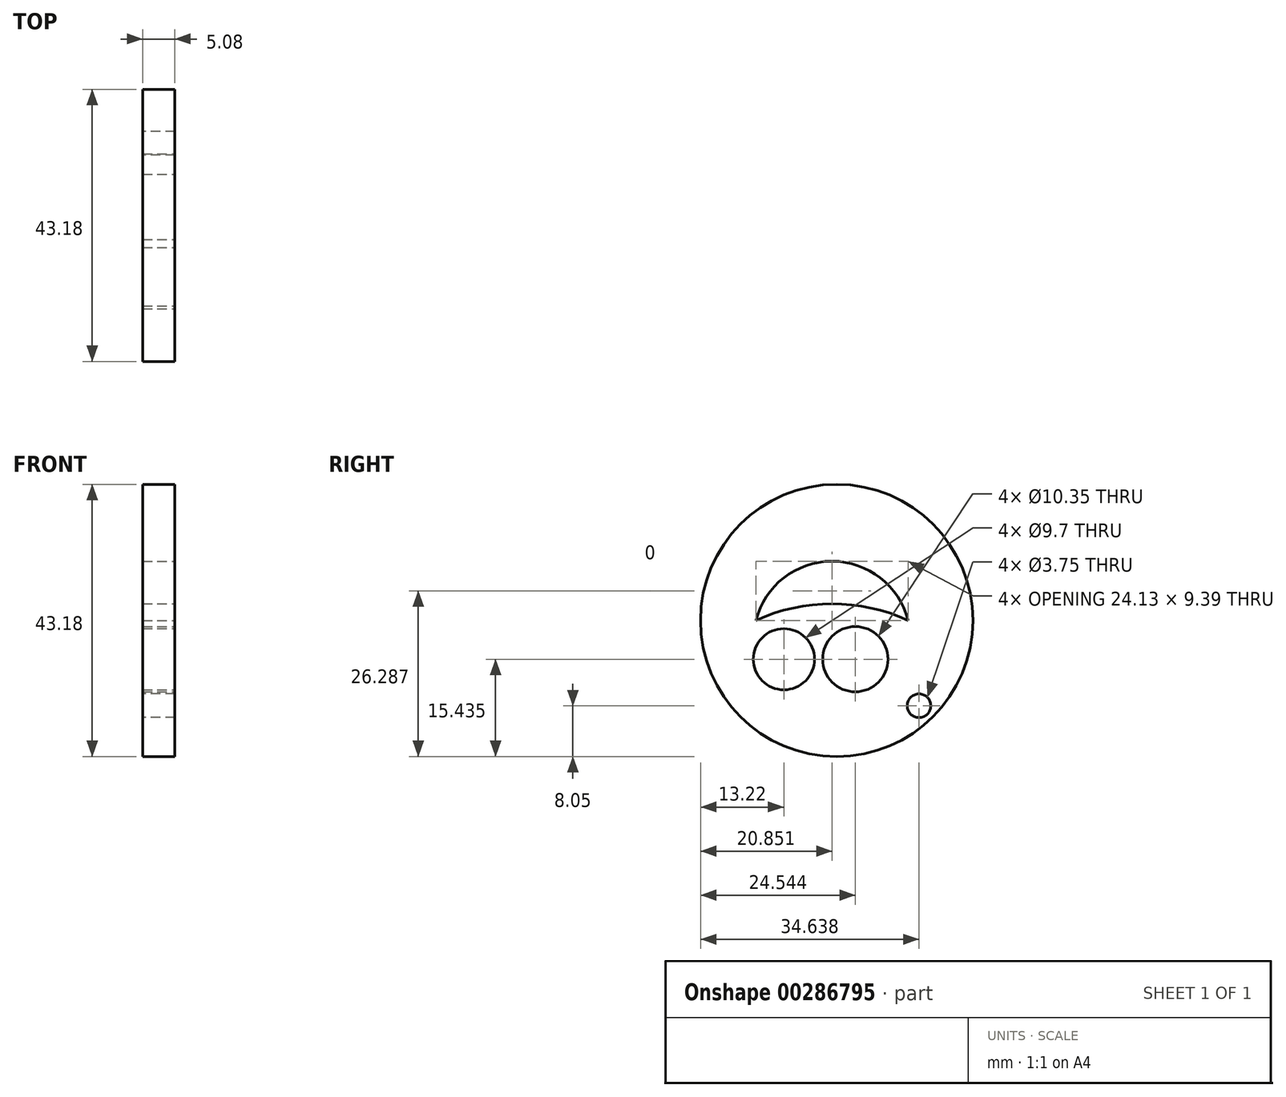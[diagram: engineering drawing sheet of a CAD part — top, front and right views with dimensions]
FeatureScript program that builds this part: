
annotation { "Feature Type Name" : "Feature", "Feature Type Description" : "" }
export const myFeature = defineFeature(function(context is Context, id is Id, definition is map)
    precondition{}
    {
        {
            var Q0;
            Q0=qCreatedBy(makeId("Right.planeOp"),FACE);
            var sketch = newSketch(context, id + "F0", { "sketchPlane" : qUnion([Q0])});
            skCircle(sketch, "E0", {"center": v(0, 0) * mm, "radius": 21.59 * mm});
            skSolve(sketch);
        }
        {
            var Q0;
            Q0 = qSketchRegion(id + "F0", true);
            extrude(context, id + "F1", {"entities" : qUnion([Q0]), "depth" : 5.08 * mm});
        }
        {
            var Q0;
            Q0=makeQuery(id+"F1.opExtrude","CAP_FACE",FACE,{"disambiguationData":[OSD([sQuery(id+"F0.wireOp",EDGE,"E0")])],"isStart":false});
            var sketch = newSketch(context, id + "F2", { "sketchPlane" : qUnion([Q0])});
            skCircle(sketch, "E1", {"center": v(-8.37, -6.15) * mm, "radius": 4.85 * mm});
            skCircle(sketch, "E2", {"center": v(2.95, -6.15) * mm, "radius": 5.18 * mm});
            skArc(sketch, "E3", {"start": v(11.32, 0) * mm, "mid": v(-0.74, 9.4) * mm, "end": v(-12.8, 0) * mm});
            skArc(sketch, "E4", {"start": v(11.32, 0) * mm, "mid": v(-0.74, 2.64) * mm, "end": v(-12.8, 0) * mm});
            skSolve(sketch);
        }
        {
            var Q0;
            Q0=makeQuery(id+"F2.imprint","IMPRINT",FACE,{"disambiguationData":[TD([[makeQuery(id+"F2.imprint","IMPRINT",EDGE,{"derivedFrom":sQuery(id+"F2.wireOp",EDGE,"E3")}),1.0]])]});
            var Q1;
            Q1=makeQuery(id+"F2.imprint","IMPRINT",FACE,{"disambiguationData":[TD([[makeQuery(id+"F2.imprint","IMPRINT",EDGE,{"derivedFrom":sQuery(id+"F2.wireOp",EDGE,"E1")}),1.0]])]});
            var Q2;
            Q2=makeQuery(id+"F2.imprint","IMPRINT",FACE,{"disambiguationData":[TD([[makeQuery(id+"F2.imprint","IMPRINT",EDGE,{"derivedFrom":sQuery(id+"F2.wireOp",EDGE,"E2")}),1.0]])]});
            extrude(context, id + "F3", {"entities" : qUnion([Q0, Q1, Q2]), "operationType" : NewBodyOperationType.REMOVE, "oppositeDirection" : true, "depth" : 5.08 * mm});
        }
        {
            var Q0;
            Q0=makeQuery(id+"F1.opExtrude","CAP_FACE",FACE,{"disambiguationData":[OSD([sQuery(id+"F0.wireOp",EDGE,"E0")])],"isStart":true});
            var sketch = newSketch(context, id + "F4", { "sketchPlane" : qUnion([Q0])});
            skPoint(sketch, "E5.end.orphan", {"position": v(0.74, -26.26) * mm});
            skCircle(sketch, "E6", {"center": v(-13.05, -13.54) * mm, "radius": 1.87 * mm});
            skSolve(sketch);
        }
        {
            var Q0;
            Q0 = qSketchRegion(id + "F4", true);
            extrude(context, id + "F5", {"entities" : qUnion([Q0]), "operationType" : NewBodyOperationType.REMOVE, "oppositeDirection" : true, "depth" : 5.08 * mm});
        }
    });
